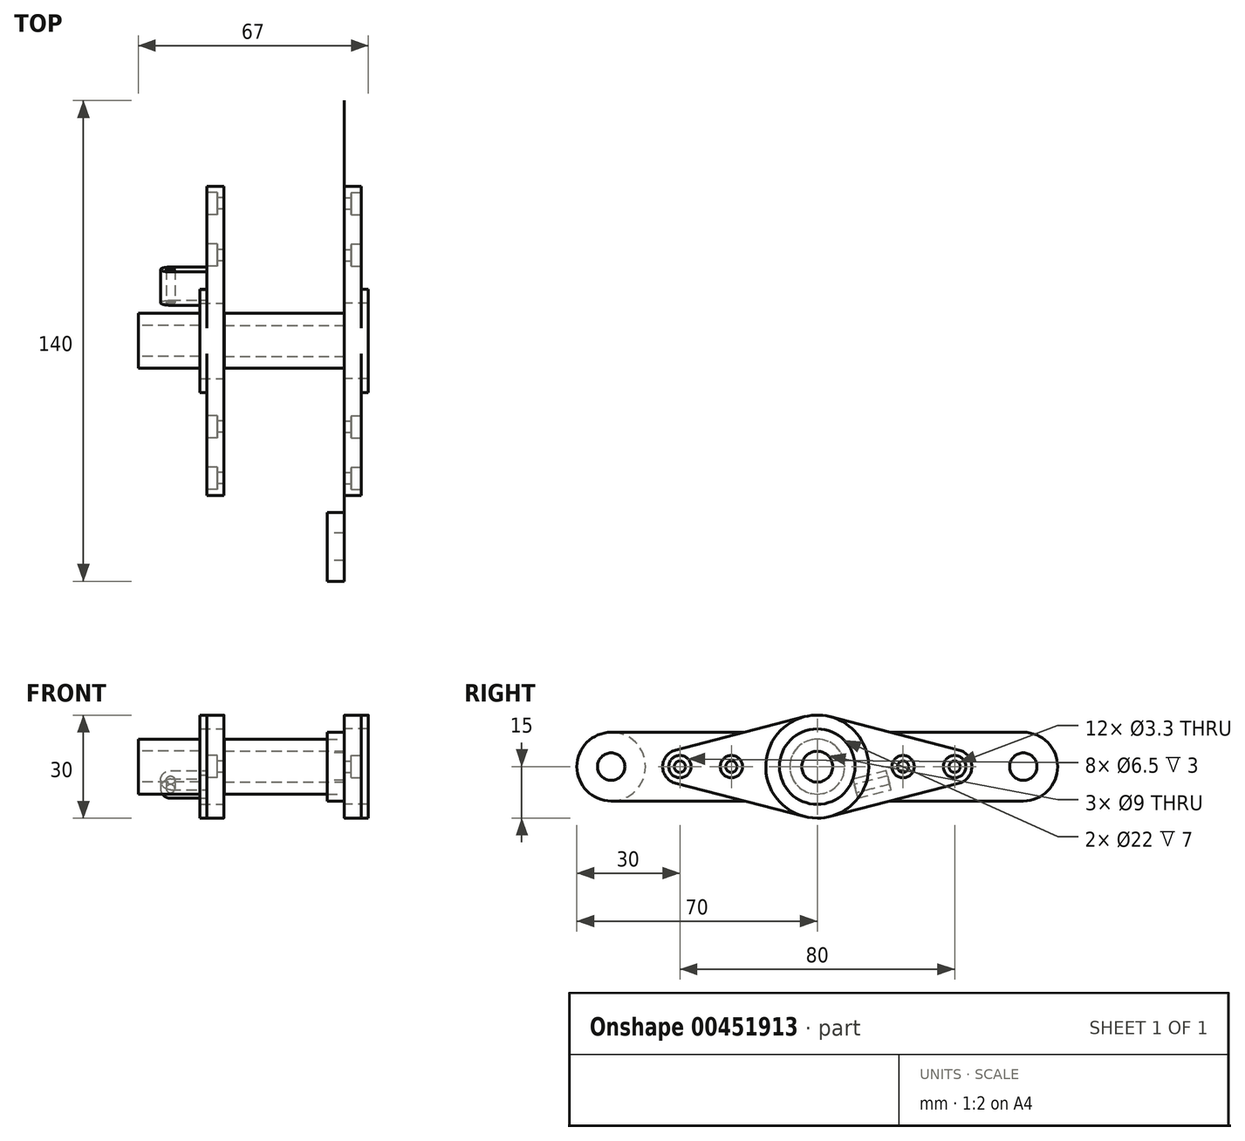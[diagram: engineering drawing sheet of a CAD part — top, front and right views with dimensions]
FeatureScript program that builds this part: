
annotation { "Feature Type Name" : "Feature", "Feature Type Description" : "" }
export const myFeature = defineFeature(function(context is Context, id is Id, definition is map)
    precondition{}
    {
        {
            var Q0;
            Q0=qCreatedBy(makeId("Right.planeOp"),FACE);
            var sketch = newSketch(context, id + "F0", { "sketchPlane" : qUnion([Q0])});
            skCircle(sketch, "E0", {"center": v(0, 0) * mm, "radius": 15 * mm});
            skCircle(sketch, "E1", {"center": v(0, 0) * mm, "radius": 11 * mm});
            skLineSegment(sketch, "E2", {"start": v(41.25, 4.84) * mm, "end": v(3.75, 14.52) * mm});
            skLineSegment(sketch, "E3", {"start": v(41.25, -4.84) * mm, "end": v(3.75, -14.52) * mm});
            skArc(sketch, "E4", {"start": v(41.25, -4.84) * mm, "mid": v(45, 0) * mm, "end": v(41.25, 4.84) * mm});
            skPoint(sketch, "E5.orphan", {"position": v(60, 0) * mm});
            skArc(sketch, "E6", {"start": v(-41.25, 4.84) * mm, "mid": v(-45, 0) * mm, "end": v(-41.25, -4.84) * mm});
            skLineSegment(sketch, "E7", {"start": v(-41.25, 4.84) * mm, "end": v(-3.75, 14.52) * mm});
            skLineSegment(sketch, "E8", {"start": v(-41.25, -4.84) * mm, "end": v(-3.75, -14.52) * mm});
            skPoint(sketch, "E9", {"position": v(-27.5, 0) * mm});
            skPoint(sketch, "E10", {"position": v(27.5, 0) * mm});
            skLineSegment(sketch, "E11", {"start": v(-40, 0) * mm, "end": v(-15, 0) * mm, "construction": true});
            skLineSegment(sketch, "E12", {"start": v(40, 0) * mm, "end": v(15, 0) * mm, "construction": true});
            skSolve(sketch);
        }
        {
            var Q0;
            Q0=makeQuery(id+"F0.imprint","IMPRINT",FACE,{"disambiguationData":[TD([[makeQuery(id+"F0.imprint","IMPRINT",EDGE,{"derivedFrom":sQuery(id+"F0.wireOp",EDGE,"E1")}),-1.0]])]});
            extrude(context, id + "F1", {"entities" : qUnion([Q0]), "depth" : 7 * mm});
        }
        {
            var Q0;
            Q0=makeQuery(id+"F0.imprint","IMPRINT",FACE,{"disambiguationData":[TD([[makeQuery(id+"F0.imprint","IMPRINT",EDGE,{"derivedFrom":sQuery(id+"F0.wireOp",EDGE,"E6")}),1.0]])]});
            var Q1;
            {var subQ0=sQuery(id+"F0.wireOp",EDGE,"E2");Q1=makeQuery(id+"F0.imprint","IMPRINT",FACE,{"disambiguationData":[TD([[makeQuery(id+"F0.imprint","IMPRINT",EDGE,{"derivedFrom":subQ0}),1.0]])]});}
            extrude(context, id + "F2", {"entities" : qUnion([Q0, Q1]), "operationType" : NewBodyOperationType.ADD, "depth" : 5 * mm});
        }
        {
            var Q0;
            {var subQ0=sQuery(id+"F0.wireOp",EDGE,"E0");Q0=makeQuery(id+"F2.boolean.opBoolean","MERGE",FACE,{"derivedFrom":[makeQuery(id+"F1.opExtrude","CAP_FACE",FACE,{"disambiguationData":[OSD([subQ0,sQuery(id+"F0.wireOp",EDGE,"E1")])],"isStart":true}),makeQuery(id+"F2.opExtrude","CAP_FACE",FACE,{"disambiguationData":[OSD([subQ0,sQuery(id+"F0.wireOp",EDGE,"E6"),sQuery(id+"F0.wireOp",EDGE,"E7"),sQuery(id+"F0.wireOp",EDGE,"E8")])],"isStart":true}),makeQuery(id+"F2.opExtrude","CAP_FACE",FACE,{"disambiguationData":[OSD([subQ0,sQuery(id+"F0.wireOp",EDGE,"E2"),sQuery(id+"F0.wireOp",EDGE,"E3"),sQuery(id+"F0.wireOp",EDGE,"E4")])],"isStart":true})]});}
            var sketch = newSketch(context, id + "F3", { "sketchPlane" : qUnion([Q0])});
            skArc(sketch, "E13", {"start": v(-3.75, -14.52) * mm, "mid": v(0, -15) * mm, "end": v(3.75, -14.52) * mm});
            skLineSegment(sketch, "E14.bottom", {"start": v(60, 10) * mm, "end": v(21.27, 10) * mm});
            skLineSegment(sketch, "E14.top", {"start": v(60, -10) * mm, "end": v(21.27, -10) * mm});
            skLineSegment(sketch, "E15", {"start": v(-21.27, 10) * mm, "end": v(-3.75, 14.52) * mm});
            skLineSegment(sketch, "E16", {"start": v(3.75, 14.52) * mm, "end": v(21.27, 10) * mm});
            skLineSegment(sketch, "E17", {"start": v(-21.27, -10) * mm, "end": v(-3.75, -14.52) * mm});
            skLineSegment(sketch, "E18", {"start": v(3.75, -14.52) * mm, "end": v(21.27, -10) * mm});
            skLineSegment(sketch, "E19.trimOffspring", {"start": v(-21.27, 10) * mm, "end": v(-60, 10) * mm});
            skLineSegment(sketch, "E20.trimOffspring", {"start": v(-21.27, -10) * mm, "end": v(-60, -10) * mm});
            skArc(sketch, "E21.trimOffspring", {"start": v(3.75, 14.52) * mm, "mid": v(0, 15) * mm, "end": v(-3.75, 14.52) * mm});
            skArc(sketch, "E22", {"start": v(-60, 10) * mm, "mid": v(-70, 0) * mm, "end": v(-60, -10) * mm});
            skPoint(sketch, "E22.centerSnap0", {"position": v(-119.08, 0) * mm});
            skArc(sketch, "E23", {"start": v(60, -10) * mm, "mid": v(70, 0) * mm, "end": v(60, 10) * mm});
            skPoint(sketch, "E24.orphan", {"position": v(-119.08, 10) * mm});
            skPoint(sketch, "E25.orphan", {"position": v(-119.08, -10) * mm});
            skPoint(sketch, "E26.orphan", {"position": v(119.08, -10) * mm});
            skPoint(sketch, "E27.orphan", {"position": v(119.08, 10) * mm});
            skCircle(sketch, "E28", {"center": v(-60, 0) * mm, "radius": 4 * mm});
            skCircle(sketch, "E29", {"center": v(60, 0) * mm, "radius": 4 * mm});
            skCircle(sketch, "E30", {"center": v(0, 0) * mm, "radius": 4.5 * mm});
            skSolve(sketch);
        }
        {
            var Q0;
            Q0=qSketchRegion(id+"F3",true);
            extrude(context, id + "F4", {"entities" : qUnion([Q0]), "depth" : 1 / 203.2 * mm});
        }
        {
            var Q0;
            Q0=makeQuery(id+"F2.opExtrude","CAP_FACE",FACE,{"disambiguationData":[OSD([sQuery(id+"F0.wireOp",EDGE,"E0"),sQuery(id+"F0.wireOp",EDGE,"E6"),sQuery(id+"F0.wireOp",EDGE,"E7"),sQuery(id+"F0.wireOp",EDGE,"E8")])],"isStart":false});
            var sketch = newSketch(context, id + "F5", { "sketchPlane" : qUnion([Q0])});
            skPoint(sketch, "E31", {"position": v(-40, 0) * mm});
            skPoint(sketch, "E32", {"position": v(40, 0) * mm});
            skLineSegment(sketch, "E33", {"start": v(-40, 0) * mm, "end": v(-15, 0) * mm, "construction": true});
            skLineSegment(sketch, "E34", {"start": v(40, 0) * mm, "end": v(15, 0) * mm, "construction": true});
            skPoint(sketch, "E35", {"position": v(-25, 0) * mm});
            skPoint(sketch, "E36", {"position": v(25, 0) * mm});
            skSolve(sketch);
        }
        {
            var Q0;
            Q0=sQuery(id+"F5.wireOp",VERTEX,"E31");
            var Q1;
            Q1=sQuery(id+"F5.wireOp",VERTEX,"E32");
            var Q2;
            Q2=sQuery(id+"F5.wireOp",VERTEX,"E35");
            var Q3;
            Q3=sQuery(id+"F5.wireOp",VERTEX,"E36");
            var Q4;
            Q4=makeQuery(id+"F1.opExtrude","SWEPT_BODY",BODY,{"disambiguationData":[OSD([sQuery(id+"F0.wireOp",EDGE,"E0"),sQuery(id+"F0.wireOp",EDGE,"E1")])]});
            var Q5;
            Q5=makeQuery(id+"F4.opExtrude","SWEPT_BODY",BODY,{"disambiguationData":[OSD([sQuery(id+"F3.wireOp",EDGE,"E13"),sQuery(id+"F3.wireOp",EDGE,"E14.bottom"),sQuery(id+"F3.wireOp",EDGE,"E14.top"),sQuery(id+"F3.wireOp",EDGE,"E15"),sQuery(id+"F3.wireOp",EDGE,"E16"),sQuery(id+"F3.wireOp",EDGE,"E17"),sQuery(id+"F3.wireOp",EDGE,"E18"),sQuery(id+"F3.wireOp",EDGE,"E19.trimOffspring"),sQuery(id+"F3.wireOp",EDGE,"E20.trimOffspring"),sQuery(id+"F3.wireOp",EDGE,"E21.trimOffspring"),sQuery(id+"F3.wireOp",EDGE,"E22"),sQuery(id+"F3.wireOp",EDGE,"E23"),sQuery(id+"F3.wireOp",EDGE,"E28"),sQuery(id+"F3.wireOp",EDGE,"E29"),sQuery(id+"F3.wireOp",EDGE,"E30")])]});
            hole(context, id + "F6", {"style" : HoleStyle.C_BORE, "endStyle" : HoleEndStyle.BLIND, "standardTappedOrClearance" : lookupTablePath({ "standard" : "ISO", "fit" : "Normal", "size" : "M3", "type" : "Clearance" }), "standardBlindInLast" : lookupTablePath({ "fit" : "Standard", "standard" : "ISO", "size" : "M3", "type" : "Clearance" }), "holeDiameter" : 3.3 * mm, "cBoreDiameter" : 6.5 * mm, "cBoreDepth" : 3 * mm, "holeDepth" : 16 * mm, "tappedDepth" : 12 * mm, "tapClearance" : 3, "locations" : qUnion([Q0, Q1, Q2, Q3]), "scope" : qUnion([Q4, Q5])});
        }
        {
            var Q0;
            Q0=makeQuery(id+"F4.opExtrude","CAP_FACE",FACE,{"disambiguationData":[OSD([sQuery(id+"F3.wireOp",EDGE,"E13"),sQuery(id+"F3.wireOp",EDGE,"E14.bottom"),sQuery(id+"F3.wireOp",EDGE,"E14.top"),sQuery(id+"F3.wireOp",EDGE,"E15"),sQuery(id+"F3.wireOp",EDGE,"E16"),sQuery(id+"F3.wireOp",EDGE,"E17"),sQuery(id+"F3.wireOp",EDGE,"E18"),sQuery(id+"F3.wireOp",EDGE,"E19.trimOffspring"),sQuery(id+"F3.wireOp",EDGE,"E20.trimOffspring"),sQuery(id+"F3.wireOp",EDGE,"E21.trimOffspring"),sQuery(id+"F3.wireOp",EDGE,"E22"),sQuery(id+"F3.wireOp",EDGE,"E23"),sQuery(id+"F3.wireOp",EDGE,"E28"),sQuery(id+"F3.wireOp",EDGE,"E29"),sQuery(id+"F3.wireOp",EDGE,"E30")])],"isStart":false});
            var sketch = newSketch(context, id + "F7", { "sketchPlane" : qUnion([Q0])});
            skCircle(sketch, "E37", {"center": v(0, 0) * mm, "radius": 8 * mm});
            skCircle(sketch, "E38", {"center": v(0, 0) * mm, "radius": 4.5 * mm});
            skCircle(sketch, "E39", {"center": v(60, 0) * mm, "radius": 4 * mm});
            skCircle(sketch, "E40", {"center": v(60, 0) * mm, "radius": 10 * mm});
            skSolve(sketch);
        }
        {
            var Q0;
            Q0=makeQuery(id+"F7.imprint","IMPRINT",FACE,{"disambiguationData":[TD([[makeQuery(id+"F7.imprint","IMPRINT",EDGE,{"derivedFrom":sQuery(id+"F7.wireOp",EDGE,"E37")}),1.0]])]});
            extrude(context, id + "F8", {"entities" : qUnion([Q0]), "depth" : 35 * mm});
        }
        {
            var Q0;
            Q0=makeQuery(id+"F8.opExtrude","CAP_FACE",FACE,{"disambiguationData":[OSD([sQuery(id+"F7.wireOp",EDGE,"E37"),sQuery(id+"F7.wireOp",EDGE,"E38")])],"isStart":true});
            var Q1;
            Q1=makeQuery(id+"F8.opExtrude","CAP_FACE",FACE,{"disambiguationData":[OSD([sQuery(id+"F7.wireOp",EDGE,"E37"),sQuery(id+"F7.wireOp",EDGE,"E38")])],"isStart":false});
            cPlane(context, id + "F9", {"entities" : qUnion([Q0, Q1]), "cplaneType" : CPlaneType.MID_PLANE, "offset" : 25 * mm, "width" : 150 * mm, "height" : 150 * mm});
        }
        {
            var Q0;
            Q0=qCreatedBy(id+"F9.planeOp",FACE);
            cPlane(context, id + "F10", {"entities" : qUnion([Q0]), "cplaneType" : CPlaneType.OFFSET, "offset" : (25 / 2) * mm, "width" : 150 * mm, "height" : 150 * mm});
        }
        {
            var Q0;
            Q0=qCreatedBy(id+"F10.planeOp",FACE);
            var sketch = newSketch(context, id + "F11", { "sketchPlane" : qUnion([Q0])});
            skCircle(sketch, "E41", {"center": v(-60, 0) * mm, "radius": 4 * mm});
            skCircle(sketch, "E42", {"center": v(-60, 0) * mm, "radius": 10 * mm});
            skSolve(sketch);
        }
        {
            var Q0;
            Q0=makeQuery(id+"F11.imprint","IMPRINT",FACE,{"disambiguationData":[TD([[makeQuery(id+"F11.imprint","IMPRINT",EDGE,{"derivedFrom":sQuery(id+"F11.wireOp",EDGE,"E41")}),-1.0]])]});
            var Q1;
            Q1=makeQuery(id+"F4.opExtrude","CAP_FACE",FACE,{"disambiguationData":[OSD([sQuery(id+"F3.wireOp",EDGE,"E13"),sQuery(id+"F3.wireOp",EDGE,"E14.bottom"),sQuery(id+"F3.wireOp",EDGE,"E14.top"),sQuery(id+"F3.wireOp",EDGE,"E15"),sQuery(id+"F3.wireOp",EDGE,"E16"),sQuery(id+"F3.wireOp",EDGE,"E17"),sQuery(id+"F3.wireOp",EDGE,"E18"),sQuery(id+"F3.wireOp",EDGE,"E19.trimOffspring"),sQuery(id+"F3.wireOp",EDGE,"E20.trimOffspring"),sQuery(id+"F3.wireOp",EDGE,"E21.trimOffspring"),sQuery(id+"F3.wireOp",EDGE,"E22"),sQuery(id+"F3.wireOp",EDGE,"E23"),sQuery(id+"F3.wireOp",EDGE,"E28"),sQuery(id+"F3.wireOp",EDGE,"E29"),sQuery(id+"F3.wireOp",EDGE,"E30")])],"isStart":false});
            extrude(context, id + "F12", {"entities" : qUnion([Q0]), "endBound" : BoundingType.UP_TO_SURFACE, "endBoundEntityFace" : qUnion([Q1]), "depth" : 5 * mm});
        }
        {
            var Q0;
            Q0=makeQuery(id+"F1.opExtrude","SWEPT_BODY",BODY,{"disambiguationData":[OSD([sQuery(id+"F0.wireOp",EDGE,"E0"),sQuery(id+"F0.wireOp",EDGE,"E1")])]});
            var Q1;
            Q1=qCreatedBy(id+"F9.planeOp",FACE);
            mirror(context, id + "F13", {"entities" : qUnion([Q0]), "mirrorPlane" : qUnion([Q1])});
        }
        {
            var Q0;
            Q0=makeQuery(id+"F13.opPattern","COPY",FACE,{"derivedFrom":makeQuery(id+"F2.opExtrude","CAP_FACE",FACE,{"disambiguationData":[OSD([sQuery(id+"F0.wireOp",EDGE,"E0"),sQuery(id+"F0.wireOp",EDGE,"E2"),sQuery(id+"F0.wireOp",EDGE,"E3"),sQuery(id+"F0.wireOp",EDGE,"E4")])],"isStart":false}),"instanceName":"1"});
            var sketch = newSketch(context, id + "F14", { "sketchPlane" : qUnion([Q0])});
            skCircle(sketch, "E43", {"center": v(0, 0) * mm, "radius": 9 * mm, "construction": true});
            skLineSegment(sketch, "E44", {"start": v(-29.94, -1.56) * mm, "end": v(-2.25, -8.71) * mm, "construction": true});
            skLineSegment(sketch, "E45", {"start": v(-21.51, -6.72) * mm, "end": v(-20.07, -1.13) * mm});
            skLineSegment(sketch, "E46", {"start": v(-20.07, -1.13) * mm, "end": v(-10.38, -3.63) * mm});
            skLineSegment(sketch, "E47", {"start": v(-10.38, -3.63) * mm, "end": v(-11.83, -9.22) * mm});
            skLineSegment(sketch, "E48", {"start": v(-11.83, -9.22) * mm, "end": v(-21.51, -6.72) * mm});
            skSolve(sketch);
        }
        {
            var Q0;
            Q0=qSketchRegion(id+"F14",true);
            extrude(context, id + "F15", {"entities" : qUnion([Q0]), "operationType" : NewBodyOperationType.ADD, "depth" : 25 * mm});
        }
        {
            var Q0;
            Q0=makeQuery(id+"F15.opExtrude","SWEPT_FACE",FACE,{"disambiguationData":[OSD([sQuery(id+"F14.wireOp",EDGE,"E47")])]});
            var sketch = newSketch(context, id + "F16", { "sketchPlane" : qUnion([Q0])});
            skArc(sketch, "E49", {"start": v(-50.6, -6.11) * mm, "mid": v(-53.49, -9) * mm, "end": v(-50.6, -11.89) * mm});
            skCircle(sketch, "E50", {"center": v(-50.6, -9) * mm, "radius": 1.25 * mm});
            skLineSegment(sketch, "E51.bottom", {"start": v(-79.82, -25.28) * mm, "end": v(-50.6, -25.28) * mm});
            skLineSegment(sketch, "E51.top", {"start": v(-79.82, 4.34) * mm, "end": v(-50.6, 4.34) * mm});
            skLineSegment(sketch, "E51.left", {"start": v(-79.82, -25.28) * mm, "end": v(-79.82, 4.34) * mm});
            skLineSegment(sketch, "E51.right", {"start": v(-50.6, -25.28) * mm, "end": v(-50.6, -11.89) * mm});
            skLineSegment(sketch, "E52.trimOffspring", {"start": v(-50.6, -6.11) * mm, "end": v(-50.6, 4.34) * mm});
            skSolve(sketch);
        }
        {
            var Q0;
            Q0=qSketchRegion(id+"F16",true);
            extrude(context, id + "F17", {"entities" : qUnion([Q0]), "operationType" : NewBodyOperationType.REMOVE, "oppositeDirection" : true, "depth" : 25 * mm});
        }
        {
            var Q0;
            Q0=qCreatedBy(id+"F9.planeOp",FACE);
            cPlane(context, id + "F18", {"entities" : qUnion([Q0]), "cplaneType" : CPlaneType.OFFSET, "offset" : 42.5 * mm, "oppositeDirection" : true, "width" : 150 * mm, "height" : 150 * mm});
        }
        {
            var Q0;
            Q0=qCreatedBy(id+"F18.planeOp",FACE);
            var sketch = newSketch(context, id + "F19", { "sketchPlane" : qUnion([Q0])});
            skCircle(sketch, "E53", {"center": v(0, 0) * mm, "radius": 8 * mm});
            skCircle(sketch, "E54", {"center": v(0, 0) * mm, "radius": 4.5 * mm});
            skSolve(sketch);
        }
        {
            var Q0;
            Q0=qSketchRegion(id+"F19",true);
            var Q1;
            Q1=makeQuery(id+"F13.opPattern","COPY",FACE,{"derivedFrom":makeQuery(id+"F1.opExtrude","CAP_FACE",FACE,{"disambiguationData":[OSD([sQuery(id+"F0.wireOp",EDGE,"E0"),sQuery(id+"F0.wireOp",EDGE,"E1")])],"isStart":false}),"instanceName":"1"});
            extrude(context, id + "F20", {"entities" : qUnion([Q0]), "endBound" : BoundingType.UP_TO_SURFACE, "endBoundEntityFace" : qUnion([Q1]), "depth" : 17.5 * mm});
        }
    });
